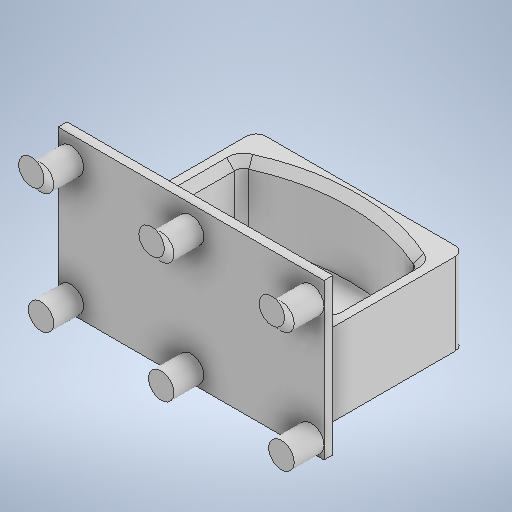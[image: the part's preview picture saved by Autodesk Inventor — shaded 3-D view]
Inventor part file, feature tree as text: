
AUTODESK INVENTOR PART (.ipt)
format: ipt  version: 2025.2 (Build 292293000, 293)  size: 461,312 bytes
history: native  units: mm
features: sketch x7, extrude x6, other x3, pattern_linear x3, fillet x3, chamfer x3, move_body x2, loft x1, delete_face x1, direct_edit x1, projected_geometry x1
ambient origin geometry x8: Origin, YZ Plane, XZ Plane, XY Plane, X Axis, Y Axis, Z Axis, Center Point
bodies: Body1 (feature_tree)
feature tree (31):
  other  "Твердое тело1"
  extrude  "Выдавливание1"  Depth=55.2mm
  extrude  "Выдавливание2"  Depth=2.0mm
  pattern_linear  "Прямоуг.массив1"  Spacing1=6.2mm  [1 undecoded]
  extrude  "Выдавливание3"  Depth=2.0mm
  extrude  "Выдавливание4"  Depth=2.0mm
  fillet  "Сопряжение1"  Radius=32.25mm
  pattern_linear  "Прямоуг.массив2"  Spacing1=0.0mm  [1 undecoded]
  fillet  "Сопряжение2"  Radius=36.5mm
  other  "РабПлоскость1"
  loft  "Лофт1"
  pattern_linear  "Прямоуг.массив3"  Spacing1=0.0mm  [1 undecoded]
  extrude  "Extrusion6"  Depth=2.0mm
  delete_face  "Delete Face1"
  extrude  "Extrusion7"  Depth=2.0mm
  fillet  "Fillet3"  Radius=10.0mm
  chamfer  "Chamfer3"  Distance=10.0mm
  direct_edit  "Direct Edit1"
  chamfer  "Фаска1"  Distance=28.9mm
  chamfer  "Фаска2"  Distance=2.0mm
  sketch  "Эскиз1"
  sketch  "Эскиз2"
  sketch  "Эскиз3"
  sketch  "Эскиз4"
  sketch  "Эскиз7"
  other  "Ребра1"
  sketch  "Sketch10"  dims[d0=1.85mm d1=0.0mm d2=55.2mm]
  projected_geometry  "Projected Loop4"
  sketch  "Sketch11"  dims[d3=32.25mm d4=5.3mm d13=6.2mm d14=0.0mm d18=20.0mm d20=24.95mm d22=32.25mm d23=0.0mm d27=36.5mm d28=30.25mm d29=0.0mm d31=26.5mm d32=2.0mm d33=10.0mm d35=38.9mm d36=10.0mm d38=28.9mm d39=2.0mm d40=6.95mm d41=31.3mm d42=45.0deg d43=6.95mm d44=31.3mm d45=45.0deg d46=41.3mm d47=33.3mm d51=2.0mm d52=30.0mm d54=24.95mm d55=2.4mm d56=2.4mm d59=2.0mm d60=5.3mm d61=2.0mm d62=0.0mm d63=90.0deg d64=0.0mm d65=90.0deg d67=30.0mm d69=24.95mm d70=15.25mm d71=0.0mm d73=18.0mm d74=15.25mm d75=0.0mm d76=2.0mm d77=1.6mm d78=2.0mm d79=45.0deg d80=0.0mm d81=0.0mm d82=1.0mm d83=0.0mm d84=0.0mm d85=1.0mm d50=0.5mm d53=0.872665mm]
  move_body  "Move1"
  move_body  "Move2"
note: 3 required parameter values undecoded (feature->parameter linkage not recoverable at this tier; creation-order binding heuristic only, values carry confidence <= 0.55)
